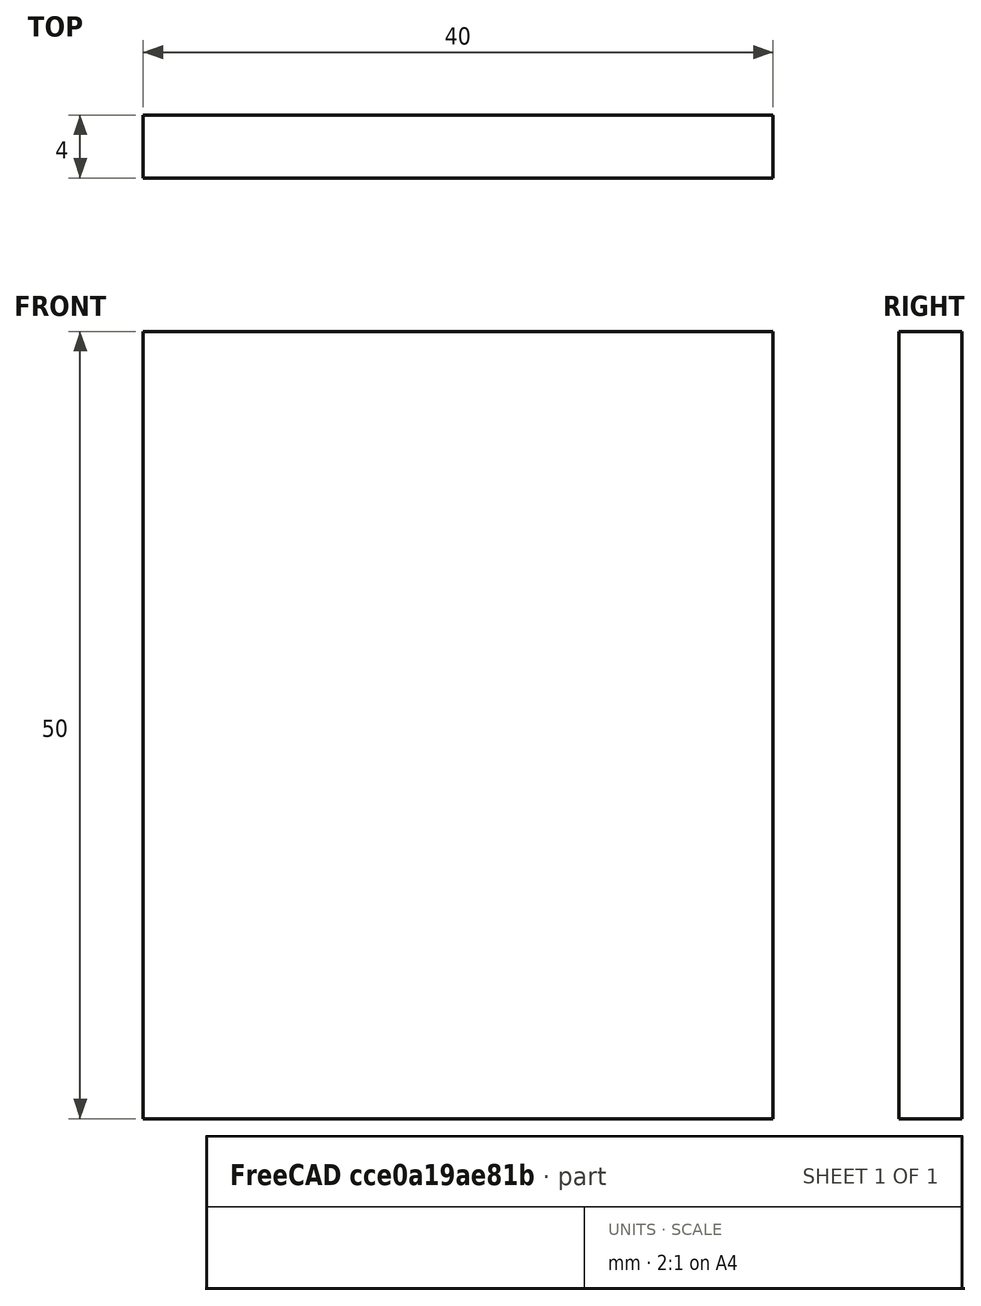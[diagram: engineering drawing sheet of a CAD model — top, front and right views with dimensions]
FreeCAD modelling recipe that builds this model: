
FCSTD DOCUMENT  (FreeCAD 0.15R4671 (Git))
Label: Flat Bar 40x4 EN10058 S235JR
License: All rights reserved
LicenseURL: http://en.wikipedia.org/wiki/All_rights_reserved
objects: Sketcher::SketchObject×1, Part::Extrusion×1
note: 2 computed .brp shape members not serialized (recipe doc carries the construction recipe); baked Part::Feature solids carry a one-line shape summary decoded from their .brp

FEATURE [Sketcher::SketchObject] Sketch
  sketch-geometry (4):
    g0: LineSegment StartX=-20 StartY=-2 StartZ=0 EndX=20 EndY=-2 EndZ=0
    g1: LineSegment StartX=20 StartY=-2 StartZ=0 EndX=20 EndY=2 EndZ=0
    g2: LineSegment StartX=20 StartY=2 StartZ=0 EndX=-20 EndY=2 EndZ=0
    g3: LineSegment StartX=-20 StartY=2 StartZ=0 EndX=-20 EndY=-2 EndZ=0
  constraints (12):
    c: Coincident(g0,g1)
    c: Coincident(g1,g2)
    c: Coincident(g2,g3)
    c: Coincident(g3,g0)
    c: Horizontal(g0)
    c: Horizontal(g2)
    c: Vertical(g1)
    c: Vertical(g3)
    c: Symmetric(g1,g2,g-2)
    c: Symmetric(g0,g1,g-1)
    c: DistanceY(g1) = 4
    c: DistanceX(g0) = 40
FEATURE [Part::Extrusion] Extrude  label="Flat Bar 40x4 EN10058 S235JR"
  Base = -> Sketch
  Dir = (0,0,50)
  Solid = true
